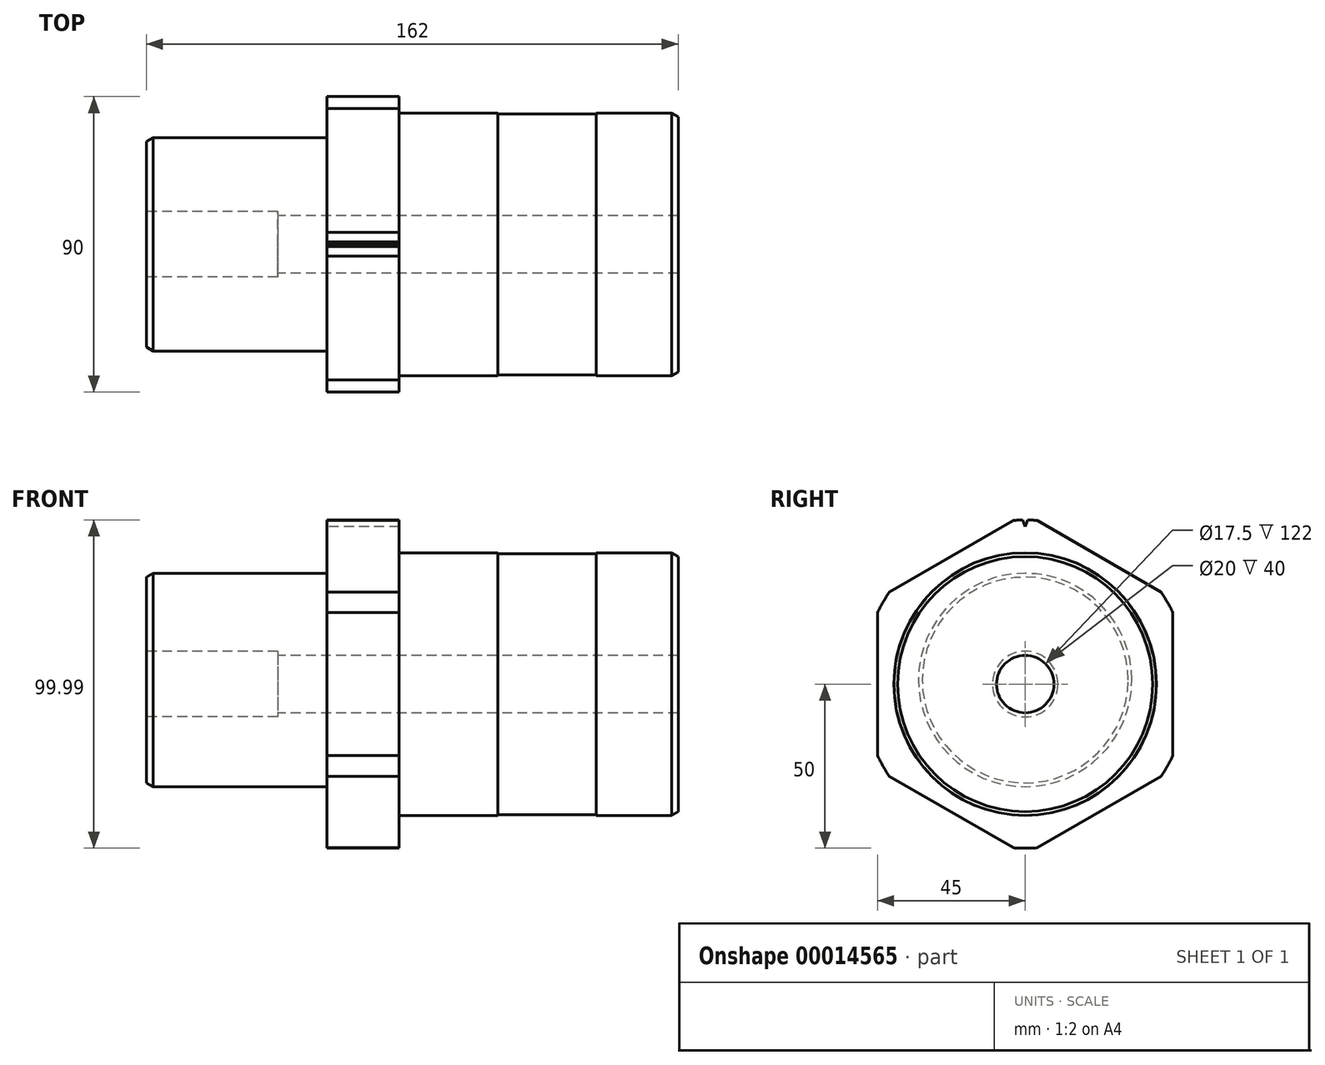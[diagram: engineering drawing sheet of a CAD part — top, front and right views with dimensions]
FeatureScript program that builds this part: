
annotation { "Feature Type Name" : "Feature", "Feature Type Description" : "" }
export const myFeature = defineFeature(function(context is Context, id is Id, definition is map)
    precondition{}
    {
        {
            var Q0;
            Q0=qCreatedBy(makeId("Right.planeOp"),FACE);
            var sketch = newSketch(context, id + "F0", { "sketchPlane" : qUnion([Q0])});
            skCircle(sketch, "E0", {"center": v(0, 0) * mm, "radius": 40 * mm});
            skCircle(sketch, "E1", {"center": v(0, 0) * mm, "radius": 8.75 * mm});
            skSolve(sketch);
        }
        {
            var Q0;
            Q0=qSketchRegion(id+"F0",true);
            extrude(context, id + "F1", {"entities" : qUnion([Q0]), "depth" : (85 - 60) * mm});
        }
        {
            var Q0;
            Q0=makeQuery(id+"F1.opExtrude","CAP_FACE",FACE,{"disambiguationData":[OSD([sQuery(id+"F0.wireOp",EDGE,"E0"),sQuery(id+"F0.wireOp",EDGE,"E1")])],"isStart":true});
            var sketch = newSketch(context, id + "F2", { "sketchPlane" : qUnion([Q0])});
            skCircle(sketch, "E2", {"center": v(0, 0) * mm, "radius": 39.75 * mm});
            skCircle(sketch, "E3.0", {"center": v(0, 0) * mm, "radius": 8.75 * mm});
            skSolve(sketch);
        }
        {
            var Q0;
            Q0=qSketchRegion(id+"F2",true);
            extrude(context, id + "F3", {"entities" : qUnion([Q0]), "operationType" : NewBodyOperationType.ADD, "depth" : 30 * mm});
        }
        {
            var Q0;
            Q0=makeQuery(id+"F3.opExtrude","CAP_FACE",FACE,{"disambiguationData":[OSD([sQuery(id+"F2.wireOp",EDGE,"E2"),sQuery(id+"F2.wireOp",EDGE,"E3.0")])],"isStart":false});
            var sketch = newSketch(context, id + "F4", { "sketchPlane" : qUnion([Q0])});
            skCircle(sketch, "E4", {"center": v(0, 0) * mm, "radius": 40 * mm});
            skCircle(sketch, "E5.0", {"center": v(0, 0) * mm, "radius": 8.75 * mm});
            skSolve(sketch);
        }
        {
            var Q0;
            Q0=qSketchRegion(id+"F4",true);
            extrude(context, id + "F5", {"entities" : qUnion([Q0]), "operationType" : NewBodyOperationType.ADD, "depth" : 30 * mm});
        }
        {
            var Q0;
            Q0=makeQuery(id+"F5.opExtrude","CAP_FACE",FACE,{"disambiguationData":[OSD([sQuery(id+"F4.wireOp",EDGE,"E4"),sQuery(id+"F4.wireOp",EDGE,"E5.0")])],"isStart":false});
            var sketch = newSketch(context, id + "F6", { "sketchPlane" : qUnion([Q0])});
            skCircle(sketch, "E6.cCircle", {"center": v(0, 0) * mm, "radius": 45 * mm, "construction": true});
            skLineSegment(sketch, "E6.0", {"start": v(-45, -21.8) * mm, "end": v(-45, 21.8) * mm});
            skLineSegment(sketch, "E6.1", {"start": v(-41.37, 28.07) * mm, "end": v(-3.63, 49.87) * mm});
            skLineSegment(sketch, "E6.2", {"start": v(3.63, 49.87) * mm, "end": v(41.37, 28.07) * mm});
            skLineSegment(sketch, "E6.3", {"start": v(45, 21.8) * mm, "end": v(45, -21.8) * mm});
            skLineSegment(sketch, "E6.4", {"start": v(41.37, -28.07) * mm, "end": v(3.63, -49.87) * mm});
            skLineSegment(sketch, "E6.5", {"start": v(-3.63, -49.87) * mm, "end": v(-41.37, -28.07) * mm});
            skPoint(sketch, "E6.0.midPoint", {"position": v(-45, 0) * mm});
            skCircle(sketch, "E7.0", {"center": v(0, 0) * mm, "radius": 8.75 * mm});
            skArc(sketch, "E8", {"start": v(-3.63, -49.87) * mm, "mid": v(0, -50) * mm, "end": v(3.63, -49.87) * mm});
            skPoint(sketch, "E9.orphan", {"position": v(-45, -25.98) * mm});
            skArc(sketch, "E10.trimOffspring", {"start": v(-45, -21.8) * mm, "mid": v(-43.3, -25) * mm, "end": v(-41.37, -28.07) * mm});
            skPoint(sketch, "E11.orphan", {"position": v(-45, 25.98) * mm});
            skArc(sketch, "E12.trimOffspring", {"start": v(-41.37, 28.07) * mm, "mid": v(-43.3, 25) * mm, "end": v(-45, 21.8) * mm});
            skPoint(sketch, "E13.orphan", {"position": v(0, 51.96) * mm});
            skArc(sketch, "E14.trimOffspring", {"start": v(3.63, 49.87) * mm, "mid": v(0, 50) * mm, "end": v(-3.63, 49.87) * mm});
            skPoint(sketch, "E15.orphan", {"position": v(45, 25.98) * mm});
            skArc(sketch, "E16.trimOffspring", {"start": v(45, 21.8) * mm, "mid": v(43.3, 25) * mm, "end": v(41.37, 28.07) * mm});
            skPoint(sketch, "E17.orphan", {"position": v(45, -25.98) * mm});
            skArc(sketch, "E18.trimOffspring", {"start": v(41.37, -28.07) * mm, "mid": v(43.3, -25) * mm, "end": v(45, -21.8) * mm});
            skPoint(sketch, "E19.orphan", {"position": v(0, -51.96) * mm});
            skSolve(sketch);
        }
        {
            var Q0;
            Q0=qSketchRegion(id+"F6",true);
            extrude(context, id + "F7", {"entities" : qUnion([Q0]), "operationType" : NewBodyOperationType.ADD, "depth" : 22 * mm});
        }
        {
            var Q0;
            Q0=makeQuery(id+"F7.opExtrude","CAP_FACE",FACE,{"disambiguationData":[OSD([sQuery(id+"F6.wireOp",EDGE,"E6.0"),sQuery(id+"F6.wireOp",EDGE,"E6.1"),sQuery(id+"F6.wireOp",EDGE,"E6.2"),sQuery(id+"F6.wireOp",EDGE,"E6.3"),sQuery(id+"F6.wireOp",EDGE,"E6.4"),sQuery(id+"F6.wireOp",EDGE,"E6.5"),sQuery(id+"F6.wireOp",EDGE,"E7.0"),sQuery(id+"F6.wireOp",EDGE,"E8"),sQuery(id+"F6.wireOp",EDGE,"E10.trimOffspring"),sQuery(id+"F6.wireOp",EDGE,"E12.trimOffspring"),sQuery(id+"F6.wireOp",EDGE,"E14.trimOffspring"),sQuery(id+"F6.wireOp",EDGE,"E16.trimOffspring"),sQuery(id+"F6.wireOp",EDGE,"E18.trimOffspring")])],"isStart":false});
            var sketch = newSketch(context, id + "F8", { "sketchPlane" : qUnion([Q0])});
            skLineSegment(sketch, "E20", {"start": v(0, 50) * mm, "end": v(0, 48) * mm, "construction": true});
            skLineSegment(sketch, "E21", {"start": v(0, 48) * mm, "end": v(-1.95, 53.35) * mm});
            skLineSegment(sketch, "E22.0.MirrorCS", {"start": v(0, 48) * mm, "end": v(1.95, 53.35) * mm});
            skLineSegment(sketch, "E23", {"start": v(-1.95, 53.35) * mm, "end": v(1.95, 53.35) * mm});
            skSolve(sketch);
        }
        {
            var Q0;
            Q0=qSketchRegion(id+"F8",true);
            extrude(context, id + "F9", {"entities" : qUnion([Q0]), "operationType" : NewBodyOperationType.REMOVE, "oppositeDirection" : true, "depth" : 25 * mm});
        }
        {
            var Q0;
            Q0=makeQuery(id+"F7.opExtrude","CAP_FACE",FACE,{"disambiguationData":[OSD([sQuery(id+"F6.wireOp",EDGE,"E6.0"),sQuery(id+"F6.wireOp",EDGE,"E6.1"),sQuery(id+"F6.wireOp",EDGE,"E6.2"),sQuery(id+"F6.wireOp",EDGE,"E6.3"),sQuery(id+"F6.wireOp",EDGE,"E6.4"),sQuery(id+"F6.wireOp",EDGE,"E6.5"),sQuery(id+"F6.wireOp",EDGE,"E7.0"),sQuery(id+"F6.wireOp",EDGE,"E8"),sQuery(id+"F6.wireOp",EDGE,"E10.trimOffspring"),sQuery(id+"F6.wireOp",EDGE,"E12.trimOffspring"),sQuery(id+"F6.wireOp",EDGE,"E14.trimOffspring"),sQuery(id+"F6.wireOp",EDGE,"E16.trimOffspring"),sQuery(id+"F6.wireOp",EDGE,"E18.trimOffspring")])],"isStart":false});
            var sketch = newSketch(context, id + "F10", { "sketchPlane" : qUnion([Q0])});
            skLineSegment(sketch, "E24", {"start": v(0, 0) * mm, "end": v(0, 1.25) * mm, "construction": true});
            skCircle(sketch, "E25", {"center": v(0, 1.25) * mm, "radius": 32.5 * mm});
            skSolve(sketch);
        }
        {
            var Q0;
            Q0=qSketchRegion(id+"F10",true);
            extrude(context, id + "F11", {"entities" : qUnion([Q0]), "operationType" : NewBodyOperationType.ADD, "depth" : 55 * mm});
        }
        {
            var Q0;
            Q0=makeQuery(id+"F11.opExtrude","CAP_FACE",FACE,{"disambiguationData":[OSD([sQuery(id+"F10.wireOp",EDGE,"E25")])],"isStart":false});
            var sketch = newSketch(context, id + "F12", { "sketchPlane" : qUnion([Q0])});
            skLineSegment(sketch, "E26", {"start": v(0, 0) * mm, "end": v(-58.41, 0) * mm, "construction": true});
            skSolve(sketch);
        }
        {
            var Q0;
            Q0=sQuery(id+"F12.wireOp",VERTEX,"E26.start");
            var Q1;
            Q1=makeQuery(id+"F1.opExtrude","SWEPT_BODY",BODY,{"disambiguationData":[OSD([sQuery(id+"F0.wireOp",EDGE,"E0"),sQuery(id+"F0.wireOp",EDGE,"E1")])]});
            hole(context, id + "F13", {"style" : HoleStyle.C_BORE, "holeDiameter" : 17.5 * mm, "cBoreDiameter" : 20 * mm, "cBoreDepth" : 40 * mm, "endStyle" : HoleEndStyle.THROUGH, "locations" : qUnion([Q0]), "scope" : qUnion([Q1])});
        }
        {
            var Q0;
            Q0=makeQuery(id+"F11.opExtrude","CAP_EDGE",EDGE,{"disambiguationData":[OSD([sQuery(id+"F10.wireOp",EDGE,"E25")])],"isStart":false});
            var Q1;
            Q1=makeQuery(id+"F1.opExtrude","CAP_EDGE",EDGE,{"disambiguationData":[OSD([sQuery(id+"F0.wireOp",EDGE,"E0")])],"isStart":false});
            chamfer(context, id + "F14", {"entities" : qUnion([Q0, Q1]), "chamferType" : ChamferType.OFFSET_ANGLE, "width" : 2 * mm, "oppositeDirection" : true, "angle" : 30 * degree, "tangentPropagation" : true});
        }
    });
